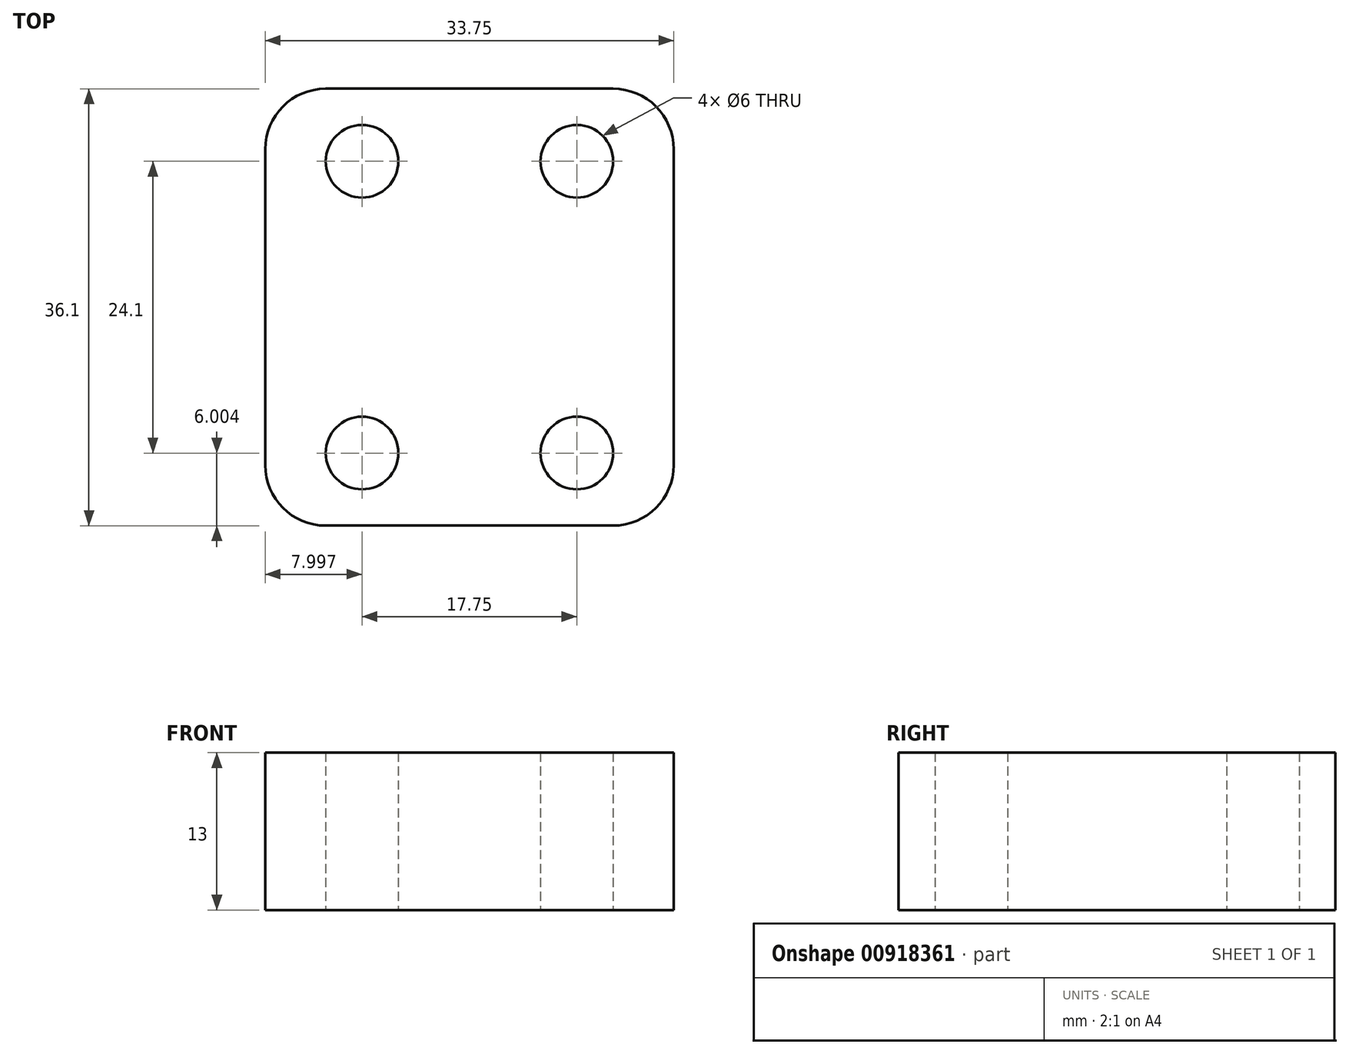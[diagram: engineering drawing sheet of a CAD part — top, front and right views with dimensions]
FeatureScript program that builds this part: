
annotation { "Feature Type Name" : "Feature", "Feature Type Description" : "" }
export const myFeature = defineFeature(function(context is Context, id is Id, definition is map)
    precondition{}
    {
        {
            var Q0;
            Q0=qCreatedBy(makeId("Top.planeOp"),FACE);
            var sketch = newSketch(context, id + "F0", { "sketchPlane" : qUnion([Q0])});
            skLineSegment(sketch, "E0.bottom", {"start": v(-50.08, 50.5) * mm, "end": v(-16.33, 50.5) * mm});
            skLineSegment(sketch, "E0.top", {"start": v(-50.08, 14.4) * mm, "end": v(-16.33, 14.4) * mm});
            skLineSegment(sketch, "E0.left", {"start": v(-50.08, 50.5) * mm, "end": v(-50.08, 14.4) * mm});
            skLineSegment(sketch, "E0.right", {"start": v(-16.33, 50.5) * mm, "end": v(-16.33, 14.4) * mm});
            skCircle(sketch, "E1", {"center": v(-42.08, 44.5) * mm, "radius": 3 * mm});
            skCircle(sketch, "E2", {"center": v(-24.33, 44.5) * mm, "radius": 3 * mm});
            skCircle(sketch, "E3", {"center": v(-42.08, 20.4) * mm, "radius": 3 * mm});
            skCircle(sketch, "E4", {"center": v(-24.33, 20.4) * mm, "radius": 3 * mm});
            skSolve(sketch);
        }
        {
            var Q0;
            Q0 = qSketchRegion(id + "F0", true);
            extrude(context, id + "F1", {"entities" : qUnion([Q0]), "depth" : 13 * mm, "offsetDistance" : 25 * mm});
        }
        {
            var Q0;
            Q0=makeQuery(id+"F1.opExtrude","SWEPT_EDGE",EDGE,{"disambiguationData":[OSD([sQuery(id+"F0.wireOp",EDGE,"E0.top"),sQuery(id+"F0.wireOp",EDGE,"E0.left")])]});
            var Q1;
            Q1=makeQuery(id+"F1.opExtrude","SWEPT_EDGE",EDGE,{"disambiguationData":[OSD([sQuery(id+"F0.wireOp",EDGE,"E0.top"),sQuery(id+"F0.wireOp",EDGE,"E0.right")])]});
            var Q2;
            Q2=makeQuery(id+"F1.opExtrude","SWEPT_EDGE",EDGE,{"disambiguationData":[OSD([sQuery(id+"F0.wireOp",EDGE,"E0.bottom"),sQuery(id+"F0.wireOp",EDGE,"E0.left")])]});
            var Q3;
            Q3=makeQuery(id+"F1.opExtrude","SWEPT_EDGE",EDGE,{"disambiguationData":[OSD([sQuery(id+"F0.wireOp",EDGE,"E0.bottom"),sQuery(id+"F0.wireOp",EDGE,"E0.right")])]});
            fillet(context, id + "F2", {"entities" : qUnion([Q0, Q1, Q2, Q3]), "radius" : 5 * mm, "tangentPropagation" : true, "allowEdgeOverflow" : false});
        }
    });
